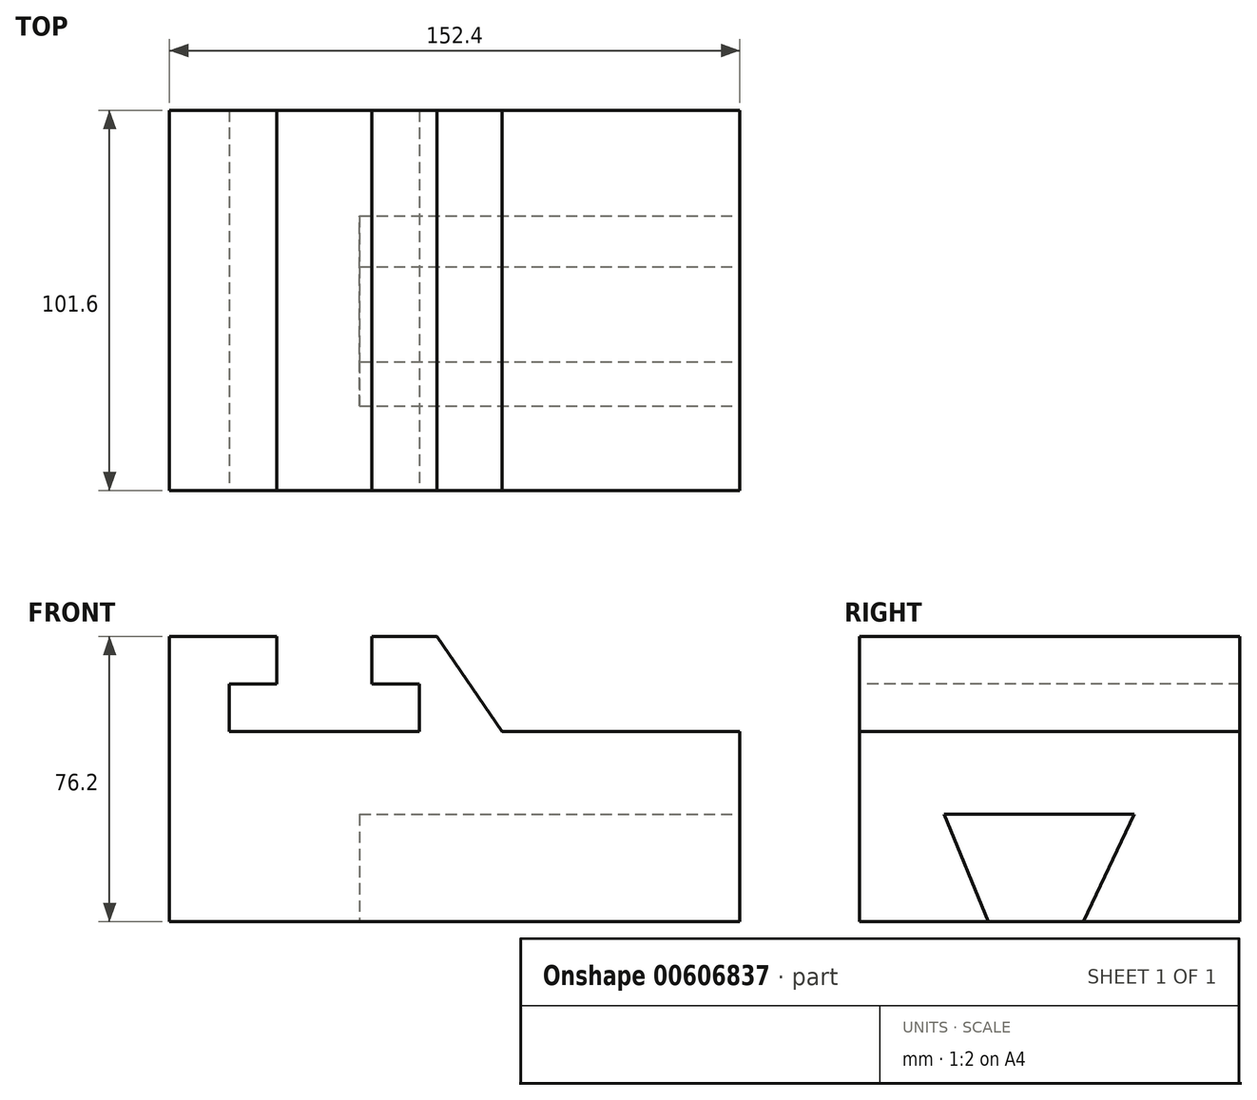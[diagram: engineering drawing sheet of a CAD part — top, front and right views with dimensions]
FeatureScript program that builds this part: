
annotation { "Feature Type Name" : "Feature", "Feature Type Description" : "" }
export const myFeature = defineFeature(function(context is Context, id is Id, definition is map)
    precondition{}
    {
        {
            var Q0;
            Q0=qCreatedBy(makeId("Front.planeOp"),FACE);
            var sketch = newSketch(context, id + "F0", { "sketchPlane" : qUnion([Q0])});
            skLineSegment(sketch, "E0.bottom", {"start": v(-79.6, -1.78) * mm, "end": v(72.8, -1.78) * mm});
            skLineSegment(sketch, "E0.top", {"start": v(-79.6, -77.98) * mm, "end": v(72.8, -77.98) * mm});
            skLineSegment(sketch, "E0.left", {"start": v(-79.6, -1.78) * mm, "end": v(-79.6, -77.98) * mm});
            skLineSegment(sketch, "E0.right", {"start": v(72.8, -1.78) * mm, "end": v(72.8, -77.98) * mm});
            skSolve(sketch);
        }
        {
            var Q0;
            Q0=makeQuery(id+"F0.imprint","IMPRINT",FACE,{"disambiguationData":[TD([[makeQuery(id+"F0.imprint","IMPRINT",EDGE,{"derivedFrom":sQuery(id+"F0.wireOp",EDGE,"E0.bottom")}),-1.0]])]});
            extrude(context, id + "F1", {"entities" : qUnion([Q0]), "oppositeDirection" : true, "depth" : 101.6 * mm, "offsetDistance" : 25.4 * mm});
        }
        {
            var Q0;
            Q0=makeQuery(id+"F1.opExtrude","CAP_FACE",FACE,{"disambiguationData":[OSD([sQuery(id+"F0.wireOp",EDGE,"E0.bottom"),sQuery(id+"F0.wireOp",EDGE,"E0.top"),sQuery(id+"F0.wireOp",EDGE,"E0.left"),sQuery(id+"F0.wireOp",EDGE,"E0.right")])],"isStart":true});
            var sketch = newSketch(context, id + "F2", { "sketchPlane" : qUnion([Q0])});
            skLineSegment(sketch, "E1", {"start": v(-50.91, -1.78) * mm, "end": v(-25.51, -1.78) * mm});
            skLineSegment(sketch, "E2", {"start": v(-25.51, -1.78) * mm, "end": v(-25.51, -14.48) * mm});
            skLineSegment(sketch, "E3", {"start": v(-25.51, -14.48) * mm, "end": v(-12.81, -14.48) * mm});
            skLineSegment(sketch, "E4", {"start": v(-12.81, -14.48) * mm, "end": v(-12.81, -27.18) * mm});
            skLineSegment(sketch, "E5", {"start": v(-12.81, -27.18) * mm, "end": v(-63.61, -27.18) * mm});
            skLineSegment(sketch, "E6", {"start": v(-63.61, -27.18) * mm, "end": v(-63.61, -14.48) * mm});
            skLineSegment(sketch, "E7", {"start": v(-63.61, -14.48) * mm, "end": v(-50.91, -14.48) * mm});
            skLineSegment(sketch, "E8", {"start": v(-50.91, -14.48) * mm, "end": v(-50.91, -1.78) * mm});
            skSolve(sketch);
        }
        {
            var Q0;
            Q0=makeQuery(id+"F2.imprint","IMPRINT",FACE,{"disambiguationData":[TD([[makeQuery(id+"F2.imprint","IMPRINT",EDGE,{"derivedFrom":sQuery(id+"F2.wireOp",EDGE,"E1")}),-1.0]])]});
            extrude(context, id + "F3", {"entities" : qUnion([Q0]), "operationType" : NewBodyOperationType.REMOVE, "oppositeDirection" : true, "depth" : 101.6 * mm, "offsetDistance" : 25.4 * mm});
        }
        {
            var Q0;
            Q0=makeQuery(id+"F1.opExtrude","SWEPT_FACE",FACE,{"disambiguationData":[OSD([sQuery(id+"F0.wireOp",EDGE,"E0.right")])]});
            var sketch = newSketch(context, id + "F4", { "sketchPlane" : qUnion([Q0])});
            skLineSegment(sketch, "E9", {"start": v(22.6, -49.33) * mm, "end": v(73.4, -49.33) * mm});
            skLineSegment(sketch, "E10", {"start": v(73.4, -49.33) * mm, "end": v(59.81, -77.98) * mm});
            skLineSegment(sketch, "E11", {"start": v(59.81, -77.98) * mm, "end": v(34.41, -77.98) * mm});
            skLineSegment(sketch, "E12", {"start": v(34.41, -77.98) * mm, "end": v(22.6, -49.33) * mm});
            skSolve(sketch);
        }
        {
            var Q0;
            Q0=makeQuery(id+"F4.imprint","IMPRINT",FACE,{"disambiguationData":[TD([[makeQuery(id+"F4.imprint","IMPRINT",EDGE,{"derivedFrom":sQuery(id+"F4.wireOp",EDGE,"E9")}),-1.0]])]});
            extrude(context, id + "F5", {"entities" : qUnion([Q0]), "operationType" : NewBodyOperationType.REMOVE, "oppositeDirection" : true, "depth" : 101.6 * mm, "offsetDistance" : 25.4 * mm});
        }
        {
            var Q0;
            Q0=makeQuery(id+"F1.opExtrude","CAP_FACE",FACE,{"disambiguationData":[OSD([sQuery(id+"F0.wireOp",EDGE,"E0.bottom"),sQuery(id+"F0.wireOp",EDGE,"E0.top"),sQuery(id+"F0.wireOp",EDGE,"E0.left"),sQuery(id+"F0.wireOp",EDGE,"E0.right")])],"isStart":true});
            var sketch = newSketch(context, id + "F6", { "sketchPlane" : qUnion([Q0])});
            skLineSegment(sketch, "E13", {"start": v(9.3, -1.78) * mm, "end": v(9.3, -27.18) * mm});
            skLineSegment(sketch, "E14", {"start": v(9.3, -27.18) * mm, "end": v(72.8, -27.18) * mm});
            skLineSegment(sketch, "E15", {"start": v(72.8, -27.18) * mm, "end": v(72.8, -1.78) * mm});
            skLineSegment(sketch, "E16", {"start": v(72.8, -1.78) * mm, "end": v(9.3, -1.78) * mm});
            skSolve(sketch);
        }
        {
            var Q0;
            Q0=makeQuery(id+"F6.imprint","IMPRINT",FACE,{"disambiguationData":[TD([[makeQuery(id+"F6.imprint","IMPRINT",EDGE,{"derivedFrom":sQuery(id+"F6.wireOp",EDGE,"E13")}),1.0]])]});
            extrude(context, id + "F7", {"entities" : qUnion([Q0]), "operationType" : NewBodyOperationType.REMOVE, "oppositeDirection" : true, "depth" : 101.6 * mm, "offsetDistance" : 25.4 * mm});
        }
        {
            var Q0;
            Q0=makeQuery(id+"F1.opExtrude","CAP_FACE",FACE,{"disambiguationData":[OSD([sQuery(id+"F0.wireOp",EDGE,"E0.bottom"),sQuery(id+"F0.wireOp",EDGE,"E0.top"),sQuery(id+"F0.wireOp",EDGE,"E0.left"),sQuery(id+"F0.wireOp",EDGE,"E0.right")])],"isStart":true});
            var sketch = newSketch(context, id + "F8", { "sketchPlane" : qUnion([Q0])});
            skLineSegment(sketch, "E17", {"start": v(-8.1, -1.78) * mm, "end": v(9.3, -1.78) * mm});
            skLineSegment(sketch, "E18", {"start": v(9.3, -1.78) * mm, "end": v(9.3, -27.18) * mm});
            skLineSegment(sketch, "E19", {"start": v(9.3, -27.18) * mm, "end": v(-8.1, -1.78) * mm});
            skSolve(sketch);
        }
        {
            var Q0;
            Q0=makeQuery(id+"F8.imprint","IMPRINT",FACE,{"disambiguationData":[TD([[makeQuery(id+"F8.imprint","IMPRINT",EDGE,{"derivedFrom":sQuery(id+"F8.wireOp",EDGE,"E17")}),-1.0]])]});
            extrude(context, id + "F9", {"entities" : qUnion([Q0]), "operationType" : NewBodyOperationType.REMOVE, "oppositeDirection" : true, "depth" : 101.6 * mm, "offsetDistance" : 25.4 * mm});
        }
    });
